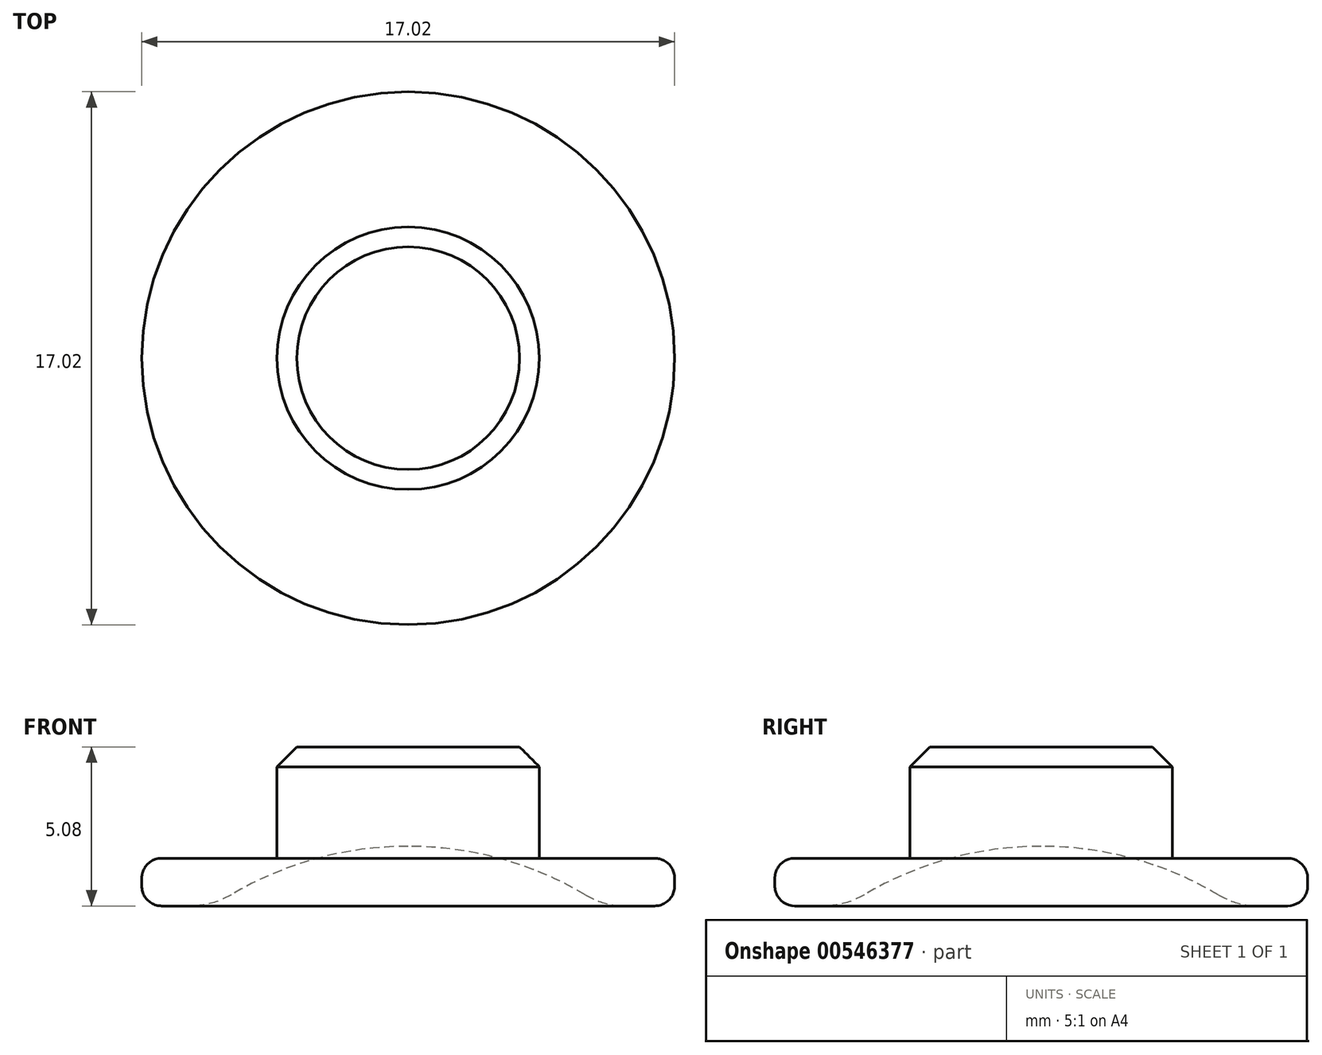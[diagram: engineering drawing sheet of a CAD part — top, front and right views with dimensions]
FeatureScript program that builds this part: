
annotation { "Feature Type Name" : "Feature", "Feature Type Description" : "" }
export const myFeature = defineFeature(function(context is Context, id is Id, definition is map)
    precondition{}
    {
        {
            var Q0;
            Q0=qCreatedBy(makeId("Top.planeOp"),FACE);
            var sketch = newSketch(context, id + "F0", { "sketchPlane" : qUnion([Q0])});
            skCircle(sketch, "E0", {"center": v(0, 0) * mm, "radius": 8.5 * mm});
            skSolve(sketch);
        }
        {
            var Q0;
            Q0=qSketchRegion(id+"F0",true);
            extrude(context, id + "F1", {"entities" : qUnion([Q0]), "depth" : 1.52 * mm, "offsetDistance" : 25.4 * mm});
        }
        {
            var Q0;
            Q0=makeQuery(id+"F1.opExtrude","CAP_FACE",FACE,{"disambiguationData":[OSD([sQuery(id+"F0.wireOp",EDGE,"E0")])],"isStart":false});
            var sketch = newSketch(context, id + "F2", { "sketchPlane" : qUnion([Q0])});
            skCircle(sketch, "E1", {"center": v(0, 0) * mm, "radius": 4.2 * mm});
            skSolve(sketch);
        }
        {
            var Q0;
            Q0=makeQuery(id+"F2.imprint","IMPRINT",FACE,{"disambiguationData":[TD([[makeQuery(id+"F2.imprint","IMPRINT",EDGE,{"derivedFrom":sQuery(id+"F2.wireOp",EDGE,"E1")}),1.0]])]});
            extrude(context, id + "F3", {"entities" : qUnion([Q0]), "operationType" : NewBodyOperationType.ADD, "depth" : 3.56 * mm, "offsetDistance" : 25.4 * mm});
        }
        {
            var Q0;
            Q0=makeQuery(id+"F1.opExtrude","CAP_EDGE",EDGE,{"disambiguationData":[OSD([sQuery(id+"F0.wireOp",EDGE,"E0")])],"isStart":false});
            var Q1;
            Q1=makeQuery(id+"F1.opExtrude","SWEPT_FACE",FACE,{"disambiguationData":[OSD([sQuery(id+"F0.wireOp",EDGE,"E0")])]});
            fillet(context, id + "F4", {"entities" : qUnion([Q0, Q1]), "radius" : 0.64 * mm, "tangentPropagation" : true, "allowEdgeOverflow" : false});
        }
        {
            var Q0;
            Q0=makeQuery(id+"F3.opExtrude","CAP_EDGE",EDGE,{"disambiguationData":[OSD([sQuery(id+"F2.wireOp",EDGE,"E1")])],"isStart":false});
            chamfer(context, id + "F5", {"entities" : qUnion([Q0]), "width" : 0.64 * mm, "tangentPropagation" : true});
        }
        {
            var Q0;
            Q0=qCreatedBy(makeId("Right.planeOp"),FACE);
            var sketch = newSketch(context, id + "F6", { "sketchPlane" : qUnion([Q0])});
            skArc(sketch, "E2", {"start": v(0, 1.9) * mm, "mid": v(-2.93, 1.51) * mm, "end": v(-5.66, 0.35) * mm});
            skLineSegment(sketch, "E3", {"start": v(-6.95, 0) * mm, "end": v(0, 0) * mm});
            skLineSegment(sketch, "E4", {"start": v(0, 0) * mm, "end": v(0, 1.9) * mm});
            skLineSegment(sketch, "E5", {"start": v(-4.45, 1.9) * mm, "end": v(0, 1.9) * mm, "construction": true});
            skArc(sketch, "E6", {"start": v(-6.95, 0) * mm, "mid": v(-6.28, 0.1) * mm, "end": v(-5.66, 0.35) * mm});
            skSolve(sketch);
        }
        {
            var Q0;
            Q0 = qSketchRegion(id + "F6", true);
            var Q1;
            Q1=sQuery(id+"F6.wireOp",EDGE,"E4");
            revolve(context, id + "F7", {"operationType" : NewBodyOperationType.REMOVE, "entities" : qUnion([Q0]), "axis" : qUnion([Q1]), "revolveType" : RevolveType.FULL, "oppositeDirection" : true});
        }
    });
